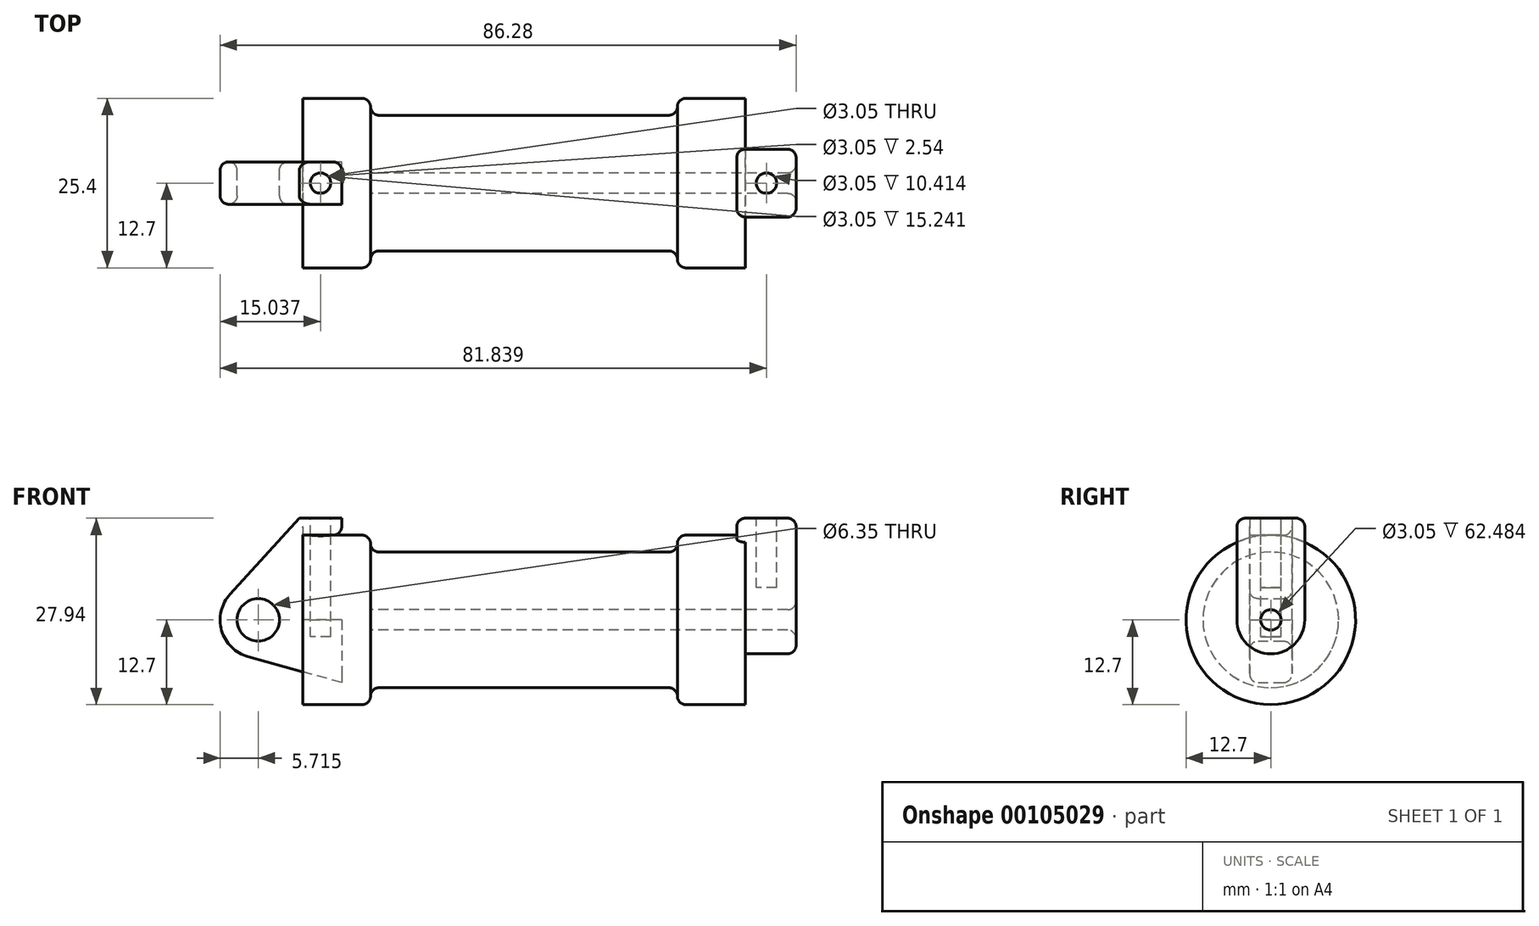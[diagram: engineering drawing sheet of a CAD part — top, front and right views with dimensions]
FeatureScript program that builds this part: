
annotation { "Feature Type Name" : "Feature", "Feature Type Description" : "" }
export const myFeature = defineFeature(function(context is Context, id is Id, definition is map)
    precondition{}
    {
        {
            var Q0;
            Q0=qCreatedBy(makeId("Front.planeOp"),FACE);
            var sketch = newSketch(context, id + "F0", { "sketchPlane" : qUnion([Q0])});
            skLineSegment(sketch, "E0", {"start": v(0, 0) * mm, "end": v(0, 12.7) * mm});
            skLineSegment(sketch, "E1", {"start": v(0, 12.7) * mm, "end": v(10.16, 12.7) * mm});
            skLineSegment(sketch, "E2", {"start": v(10.16, 12.7) * mm, "end": v(10.16, 10.16) * mm});
            skLineSegment(sketch, "E3", {"start": v(10.16, 10.16) * mm, "end": v(56.13, 10.16) * mm});
            skLineSegment(sketch, "E4", {"start": v(56.13, 10.16) * mm, "end": v(56.13, 12.7) * mm});
            skLineSegment(sketch, "E5", {"start": v(56.13, 12.7) * mm, "end": v(66.3, 12.7) * mm});
            skLineSegment(sketch, "E6", {"start": v(66.3, 12.7) * mm, "end": v(66.3, 0) * mm});
            skLineSegment(sketch, "E7", {"start": v(66.3, 0) * mm, "end": v(0, 0) * mm});
            skLineSegment(sketch, "E8", {"start": v(5.84, 15.24) * mm, "end": v(-0.5, 15.24) * mm});
            skLineSegment(sketch, "E9", {"start": v(-0.5, 15.24) * mm, "end": v(-10.88, 3.85) * mm});
            skLineSegment(sketch, "E10", {"start": v(0, 0) * mm, "end": v(-6.65, 0) * mm});
            skCircle(sketch, "E11", {"center": v(-6.65, 0) * mm, "radius": 5.72 * mm});
            skCircle(sketch, "E12", {"center": v(-6.65, 0) * mm, "radius": 3.18 * mm});
            skLineSegment(sketch, "E13", {"start": v(5.84, 15.24) * mm, "end": v(5.84, -9.4) * mm});
            skLineSegment(sketch, "E14", {"start": v(5.84, -9.4) * mm, "end": v(-8.18, -5.5) * mm});
            skSolve(sketch);
        }
        {
            var Q0;
            {var subQ0=sQuery(id+"F0.wireOp",EDGE,"E0");Q0=makeQuery(id+"F0.imprint","IMPRINT",FACE,{"disambiguationData":[TD([[makeQuery(id+"F0.imprint","IMPRINT",EDGE,{"derivedFrom":subQ0}),-1.0]])]});}
            var Q1;
            {var subQ0=sQuery(id+"F0.wireOp",EDGE,"E2");Q1=makeQuery(id+"F0.imprint","IMPRINT",FACE,{"disambiguationData":[TD([[makeQuery(id+"F0.imprint","IMPRINT",EDGE,{"derivedFrom":subQ0}),-1.0]])]});}
            var Q2;
            Q2=sQuery(id+"F0.wireOp",EDGE,"E7");
            revolve(context, id + "F1", {"entities" : qUnion([Q0, Q1]), "axis" : qUnion([Q2]), "revolveType" : RevolveType.FULL});
        }
        {
            var Q0;
            {var subQ3=sQuery(id+"F0.wireOp",EDGE,"E0");Q0=makeQuery(id+"F0.imprint","IMPRINT",FACE,{"disambiguationData":[TD([[makeQuery(id+"F0.imprint","IMPRINT",EDGE,{"derivedFrom":subQ3}),1.0]])]});}
            var Q1;
            {var subQ0=sQuery(id+"F0.wireOp",EDGE,"E14");Q1=makeQuery(id+"F0.imprint","IMPRINT",FACE,{"disambiguationData":[TD([[makeQuery(id+"F0.imprint","IMPRINT",EDGE,{"derivedFrom":subQ0}),-1.0]])]});}
            var Q2;
            {var subQ4=sQuery(id+"F0.wireOp",EDGE,"E12");Q2=makeQuery(id+"F0.imprint","IMPRINT",FACE,{"disambiguationData":[TD([[makeQuery(id+"F0.imprint","IMPRINT",EDGE,{"derivedFrom":subQ4}),-1.0]])]});}
            extrude(context, id + "F2", {"entities" : qUnion([Q0, Q1, Q2]), "endBound" : BoundingType.SYMMETRIC, "depth" : 6.35 * mm});
        }
        {
            var Q0;
            Q0=makeQuery(id+"F1.opRevolve","SWEPT_FACE",FACE,{"disambiguationData":[OSD([sQuery(id+"F0.wireOp",EDGE,"E6")])]});
            var sketch = newSketch(context, id + "F3", { "sketchPlane" : qUnion([Q0])});
            skCircle(sketch, "E15", {"center": v(0, 0) * mm, "radius": 5.08 * mm});
            skCircle(sketch, "E16", {"center": v(0, 0) * mm, "radius": 1.52 * mm});
            skLineSegment(sketch, "E17", {"start": v(-5.08, 0) * mm, "end": v(-5.08, 15.24) * mm});
            skLineSegment(sketch, "E18", {"start": v(0, 0) * mm, "end": v(5.08, 0) * mm});
            skLineSegment(sketch, "E19", {"start": v(5.08, 0) * mm, "end": v(5.08, 15.24) * mm});
            skLineSegment(sketch, "E20", {"start": v(-5.08, 15.24) * mm, "end": v(5.08, 15.24) * mm});
            skSolve(sketch);
        }
        {
            var Q0;
            {var subQ0=sQuery(id+"F3.wireOp",EDGE,"E17");var subQ1=sQuery(id+"F3.wireOp",EDGE,"E15");var subQ2=makeQuery(id+"F3.imprint","INTERSECT",VERTEX,{"derivedFrom":[subQ1,subQ0]});Q0=makeQuery(id+"F3.imprint","IMPRINT",FACE,{"disambiguationData":[TD([[makeQuery(id+"F3.imprint","IMPRINT",EDGE,{"disambiguationData":[TD([[subQ2,1.0]])],"derivedFrom":subQ1}),-1.0]])]});}
            var Q1;
            Q1=makeQuery(id+"F3.imprint","IMPRINT",FACE,{"disambiguationData":[TD([[makeQuery(id+"F3.imprint","IMPRINT",EDGE,{"derivedFrom":sQuery(id+"F3.wireOp",EDGE,"E16")}),-1.0]])]});
            var Q2;
            {var subQ0=sQuery(id+"F3.wireOp",EDGE,"E20");Q2=makeQuery(id+"F3.imprint","IMPRINT",FACE,{"disambiguationData":[TD([[makeQuery(id+"F3.imprint","IMPRINT",EDGE,{"derivedFrom":subQ0}),-1.0]])]});}
            extrude(context, id + "F4", {"entities" : qUnion([Q0, Q1, Q2]), "operationType" : NewBodyOperationType.ADD, "depth" : 7.62 * mm, "hasSecondDirection" : true, "secondDirectionOppositeDirection" : true, "secondDirectionDepth" : 1.27 * mm});
        }
        {
            var Q0;
            Q0=makeQuery(id+"F3.imprint","IMPRINT",FACE,{"disambiguationData":[TD([[makeQuery(id+"F3.imprint","IMPRINT",EDGE,{"derivedFrom":sQuery(id+"F3.wireOp",EDGE,"E16")}),1.0]])]});
            var Q1;
            Q1=makeQuery(id+"F1.opRevolve","SWEPT_FACE",FACE,{"disambiguationData":[OSD([sQuery(id+"F0.wireOp",EDGE,"E2")])]});
            extrude(context, id + "F5", {"entities" : qUnion([Q0]), "operationType" : NewBodyOperationType.REMOVE, "endBound" : BoundingType.UP_TO_SURFACE, "oppositeDirection" : true, "endBoundEntityFace" : qUnion([Q1]), "depth" : 25.4 * mm});
        }
        {
            var Q0;
            Q0=makeQuery(id+"F4.opExtrude","SWEPT_FACE",FACE,{"disambiguationData":[OSD([sQuery(id+"F3.wireOp",EDGE,"E20")])]});
            var sketch = newSketch(context, id + "F6", { "sketchPlane" : qUnion([Q0])});
            skLineSegment(sketch, "E21", {"start": v(65.02, 0) * mm, "end": v(73.91, 0) * mm, "construction": true});
            skLineSegment(sketch, "E22", {"start": v(69.47, -5.08) * mm, "end": v(69.47, 5.08) * mm, "construction": true});
            skCircle(sketch, "E23", {"center": v(69.47, 0) * mm, "radius": 1.52 * mm});
            skSolve(sketch);
        }
        {
            var Q0;
            Q0=makeQuery(id+"F6.imprint","IMPRINT",FACE,{"disambiguationData":[TD([[makeQuery(id+"F6.imprint","IMPRINT",EDGE,{"derivedFrom":sQuery(id+"F6.wireOp",EDGE,"E23")}),1.0]])]});
            extrude(context, id + "F7", {"entities" : qUnion([Q0]), "operationType" : NewBodyOperationType.REMOVE, "oppositeDirection" : true, "depth" : 10.4 * mm});
        }
        {
            var Q0;
            Q0=makeQuery(id+"F2.opExtrude","SWEPT_FACE",FACE,{"disambiguationData":[OSD([sQuery(id+"F0.wireOp",EDGE,"E8")])]});
            var sketch = newSketch(context, id + "F8", { "sketchPlane" : qUnion([Q0])});
            skLineSegment(sketch, "E24", {"start": v(-0.5, 0) * mm, "end": v(5.84, 0) * mm, "construction": true});
            skLineSegment(sketch, "E25", {"start": v(2.67, -3.18) * mm, "end": v(2.67, 3.18) * mm, "construction": true});
            skCircle(sketch, "E26", {"center": v(2.67, 0) * mm, "radius": 1.52 * mm});
            skSolve(sketch);
        }
        {
            var Q0;
            Q0=makeQuery(id+"F8.imprint","IMPRINT",FACE,{"disambiguationData":[TD([[makeQuery(id+"F8.imprint","IMPRINT",EDGE,{"derivedFrom":sQuery(id+"F8.wireOp",EDGE,"E26")}),1.0]])]});
            extrude(context, id + "F9", {"entities" : qUnion([Q0]), "operationType" : NewBodyOperationType.REMOVE, "oppositeDirection" : true, "depth" : 17.78 * mm});
        }
        {
            var Q0;
            Q0=makeQuery(id+"F4.opExtrude","CAP_EDGE",EDGE,{"disambiguationData":[OSD([sQuery(id+"F3.wireOp",EDGE,"E16")])],"isStart":false});
            var Q1;
            Q1=makeQuery(id+"F4.opExtrude","CAP_EDGE",EDGE,{"disambiguationData":[OSD([sQuery(id+"F3.wireOp",EDGE,"E15")])],"isStart":false});
            var Q2;
            Q2=makeQuery(id+"F2.opExtrude","CAP_EDGE",EDGE,{"disambiguationData":[OSD([sQuery(id+"F0.wireOp",EDGE,"E12")])],"isStart":true});
            var Q3;
            Q3=makeQuery(id+"F2.opExtrude","CAP_EDGE",EDGE,{"disambiguationData":[OSD([sQuery(id+"F0.wireOp",EDGE,"E9")])],"isStart":true});
            var Q4;
            Q4=makeQuery(id+"F2.opExtrude","CAP_EDGE",EDGE,{"disambiguationData":[OSD([sQuery(id+"F0.wireOp",EDGE,"E11")])],"isStart":true});
            var Q5;
            Q5=makeQuery(id+"F2.opExtrude","CAP_EDGE",EDGE,{"disambiguationData":[OSD([sQuery(id+"F0.wireOp",EDGE,"E1")])],"isStart":true});
            var Q6;
            {var subQ0=sQuery(id+"F0.wireOp",EDGE,"E13");Q6=makeQuery(id+"F2.opExtrude","CAP_EDGE",EDGE,{"disambiguationData":[OSD([subQ0]),TDD([makeQuery(id+"F0.imprint","IMPRINT",EDGE,{"disambiguationData":[TD([[makeQuery(id+"F0.imprint","INTERSECT",VERTEX,{"derivedFrom":[sQuery(id+"F0.wireOp",EDGE,"E8"),subQ0]}),-1.0]])],"derivedFrom":subQ0})])],"isStart":true});}
            var Q7;
            Q7=makeQuery(id+"F4.opExtrude","CAP_EDGE",EDGE,{"disambiguationData":[OSD([sQuery(id+"F3.wireOp",EDGE,"E19")])],"isStart":true});
            var Q8;
            Q8=makeQuery(id+"F4.opExtrude","CAP_EDGE",EDGE,{"disambiguationData":[OSD([sQuery(id+"F3.wireOp",EDGE,"E20")])],"isStart":true});
            var Q9;
            Q9=makeQuery(id+"F4.opExtrude","CAP_EDGE",EDGE,{"disambiguationData":[OSD([sQuery(id+"F3.wireOp",EDGE,"E17")])],"isStart":true});
            var Q10;
            Q10=makeQuery(id+"F2.opExtrude","CAP_EDGE",EDGE,{"disambiguationData":[OSD([sQuery(id+"F0.wireOp",EDGE,"E12")])],"isStart":false});
            var Q11;
            Q11=makeQuery(id+"F7.boolean.opBoolean","COPY",EDGE,{"derivedFrom":makeQuery(id+"F7.opExtrude","CAP_EDGE",EDGE,{"disambiguationData":[OSD([sQuery(id+"F6.wireOp",EDGE,"E23")])],"isStart":true})});
            var Q12;
            Q12=makeQuery(id+"F9.boolean.opBoolean","COPY",EDGE,{"derivedFrom":makeQuery(id+"F9.opExtrude","CAP_EDGE",EDGE,{"disambiguationData":[OSD([sQuery(id+"F8.wireOp",EDGE,"E26")])],"isStart":true})});
            var Q13;
            Q13=makeQuery(id+"F2.opExtrude","SWEPT_EDGE",EDGE,{"disambiguationData":[OSD([sQuery(id+"F0.wireOp",EDGE,"E1"),sQuery(id+"F0.wireOp",EDGE,"E13")])]});
            var Q14;
            Q14=makeQuery(id+"F4.opExtrude","CAP_EDGE",EDGE,{"disambiguationData":[OSD([sQuery(id+"F3.wireOp",EDGE,"E20")])],"isStart":false});
            var Q15;
            Q15=makeQuery(id+"F1.opRevolve","SWEPT_EDGE",EDGE,{"disambiguationData":[OSD([sQuery(id+"F0.wireOp",EDGE,"E1"),sQuery(id+"F0.wireOp",EDGE,"E2")])]});
            var Q16;
            Q16=makeQuery(id+"F1.opRevolve","SWEPT_EDGE",EDGE,{"disambiguationData":[OSD([sQuery(id+"F0.wireOp",EDGE,"E2"),sQuery(id+"F0.wireOp",EDGE,"E3")])]});
            var Q17;
            Q17=makeQuery(id+"F1.opRevolve","SWEPT_EDGE",EDGE,{"disambiguationData":[OSD([sQuery(id+"F0.wireOp",EDGE,"E3"),sQuery(id+"F0.wireOp",EDGE,"E4")])]});
            var Q18;
            Q18=makeQuery(id+"F1.opRevolve","SWEPT_EDGE",EDGE,{"disambiguationData":[OSD([sQuery(id+"F0.wireOp",EDGE,"E4"),sQuery(id+"F0.wireOp",EDGE,"E5")])]});
            var Q19;
            Q19=makeQuery(id+"F2.opExtrude","CAP_EDGE",EDGE,{"disambiguationData":[OSD([sQuery(id+"F0.wireOp",EDGE,"E9")])],"isStart":false});
            var Q20;
            Q20=makeQuery(id+"F2.opExtrude","CAP_EDGE",EDGE,{"disambiguationData":[OSD([sQuery(id+"F0.wireOp",EDGE,"E11")])],"isStart":false});
            var Q21;
            Q21=makeQuery(id+"F4.opExtrude","SWEPT_EDGE",EDGE,{"disambiguationData":[OSD([sQuery(id+"F3.wireOp",EDGE,"E17"),sQuery(id+"F3.wireOp",EDGE,"E20")])]});
            var Q22;
            Q22=makeQuery(id+"F4.opExtrude","SWEPT_EDGE",EDGE,{"disambiguationData":[OSD([sQuery(id+"F3.wireOp",EDGE,"E19"),sQuery(id+"F3.wireOp",EDGE,"E20")])]});
            var Q23;
            Q23=makeQuery(id+"F4.opExtrude","SWEPT_EDGE",EDGE,{"disambiguationData":[OSD([sQuery(id+"F3.wireOp",EDGE,"E15"),sQuery(id+"F3.wireOp",EDGE,"E19")])]});
            fillet(context, id + "F10", {"entities" : qUnion([Q0, Q1, Q2, Q3, Q4, Q5, Q6, Q7, Q8, Q9, Q10, Q11, Q12, Q13, Q14, Q15, Q16, Q17, Q18, Q19, Q20, Q21, Q22, Q23]), "radius" : 1.27 * mm, "tangentPropagation" : true, "allowEdgeOverflow" : false});
        }
    });
